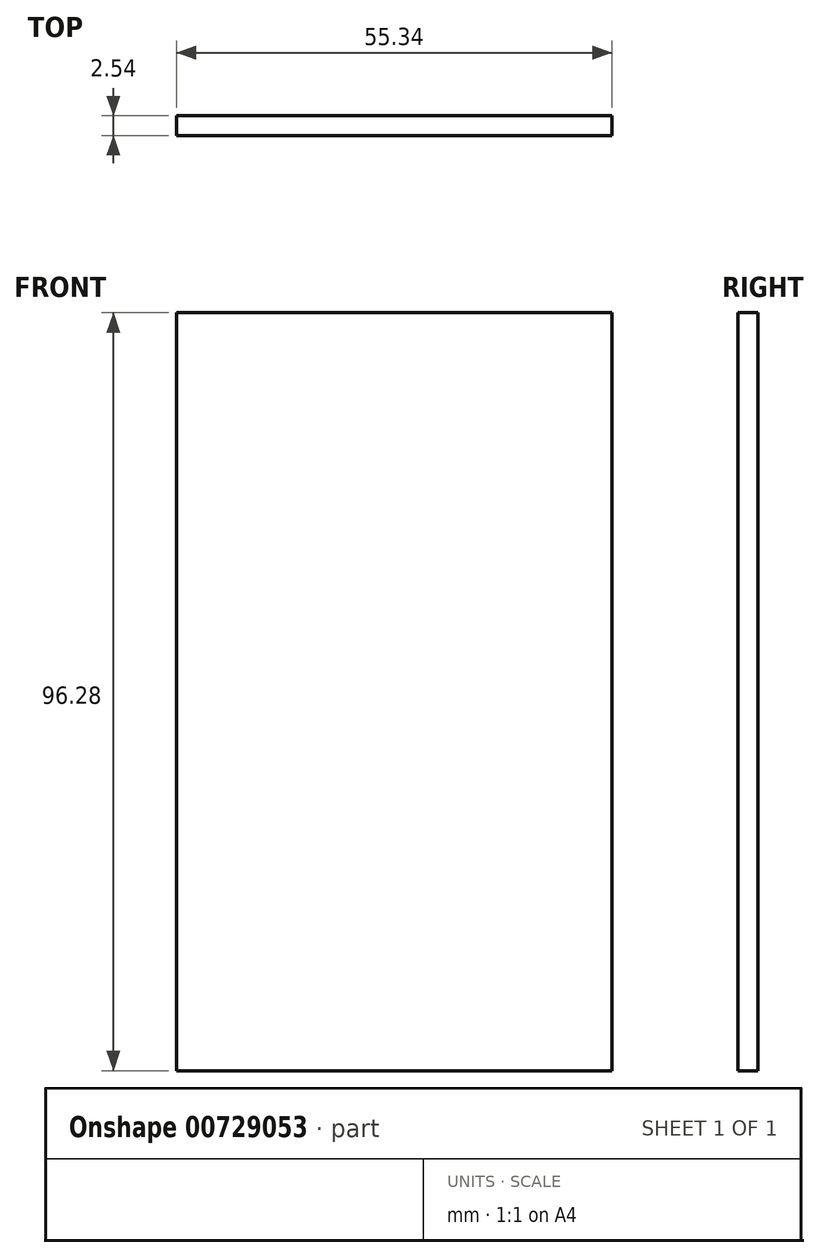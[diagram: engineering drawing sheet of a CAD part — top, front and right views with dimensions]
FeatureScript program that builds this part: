
annotation { "Feature Type Name" : "Feature", "Feature Type Description" : "" }
export const myFeature = defineFeature(function(context is Context, id is Id, definition is map)
    precondition{}
    {
        {
            var Q0;
            Q0=qCreatedBy(makeId("Front.planeOp"),FACE);
            var sketch = newSketch(context, id + "F0", { "sketchPlane" : qUnion([Q0])});
            skLineSegment(sketch, "E0.bottom", {"start": v(-32.49, 39.9) * mm, "end": v(22.85, 39.9) * mm});
            skLineSegment(sketch, "E0.top", {"start": v(-32.49, -56.38) * mm, "end": v(22.85, -56.38) * mm});
            skLineSegment(sketch, "E0.left", {"start": v(-32.49, 39.9) * mm, "end": v(-32.49, -56.38) * mm});
            skLineSegment(sketch, "E0.right", {"start": v(22.85, 39.9) * mm, "end": v(22.85, -56.38) * mm});
            skSolve(sketch);
        }
        {
            var Q0;
            Q0=makeQuery(id+"F0.imprint","IMPRINT",FACE,{"disambiguationData":[TD([[makeQuery(id+"F0.imprint","IMPRINT",EDGE,{"derivedFrom":sQuery(id+"F0.wireOp",EDGE,"E0.bottom")}),-1.0]])]});
            extrude(context, id + "F1", {"entities" : qUnion([Q0]), "depth" : 2.54 * mm, "offsetDistance" : 25.4 * mm});
        }
    });
